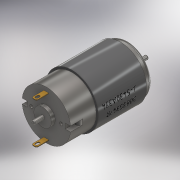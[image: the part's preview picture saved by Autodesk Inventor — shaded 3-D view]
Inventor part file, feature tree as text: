
AUTODESK INVENTOR PART (.ipt)
format: ipt  version: 2018.2 (Build 222227000, 227)  size: 288,256 bytes
history: native  units: mm
features: sketch x7, fillet x4, extrude x4, revolve x2, other x2, hole x1, plane x1
ambient origin geometry x8: Origin, YZ Plane, XZ Plane, XY Plane, X Axis, Y Axis, Z Axis, Center Point
bodies: Solid1 (feature_tree), Solid2 (feature_tree)
feature tree (21):
  sketch  "Sketch1"  dims[d0=2.23mm d1=5.6mm]
  revolve  "Revolution1"  [1 undecoded]
  revolve  "Revolution2"  [1 undecoded]
  fillet  "Fillet1"  Radius=2.1mm
  fillet  "Fillet2"  Radius=10.0mm
  hole  "Hole1"  [1 undecoded]
  extrude  "Extrusion1"  Depth=14.5mm
  fillet  "Fillet3"  Radius=27.5mm
  extrude  "Extrusion2"  TaperAngle=90.0deg  [1 undecoded]
  extrude  "Extrusion3"  Depth=2.0mm
  fillet  "Fillet4"  Radius=0.5mm
  plane  "Work Plane1"
  other  "Decal1"
  extrude  "Extrusion4"  Depth=5.0mm
  sketch  "Sketch2"  dims[d2=8.2mm d3=2.36mm d4=2.1mm d5=10.0mm]
  sketch  "Sketch3"  dims[d6=10.0mm d7=46.5mm]
  sketch  "Sketch4"  dims[d8=27.54mm d9=14.5mm d10=27.5mm]
  sketch  "Sketch5"  dims[d11=29.73mm d12=90.0deg]
  sketch  "Sketch6"  dims[d13=345.0deg d14=2.0mm d15=0.5mm]
  other  "Image1"
  sketch  "Sketch7"  dims[d16=10.5mm d17=8.0mm d18=8.0mm d19=2.0mm d20=6.0mm d21=4.0mm d22=2.0mm d23=90.0deg d24=8.0mm d25=20.594885mm d26=0.4mm d27=2.8mm d28=11.5mm d29=11.5mm d30=0.4mm d31=7.0mm d32=0.0mm d33=1.0mm d34=1.0mm d35=1.5mm d36=2.0mm d37=7.0mm d38=0.0mm d39=2.96mm d40=2.96mm d41=5.0mm d42=0.0mm d43=2.0mm d66=1.83mm d68=16.93mm d69=5.0mm d70=0.0mm]
note: 4 required parameter values undecoded (feature->parameter linkage not recoverable at this tier; creation-order binding heuristic only, values carry confidence <= 0.55)